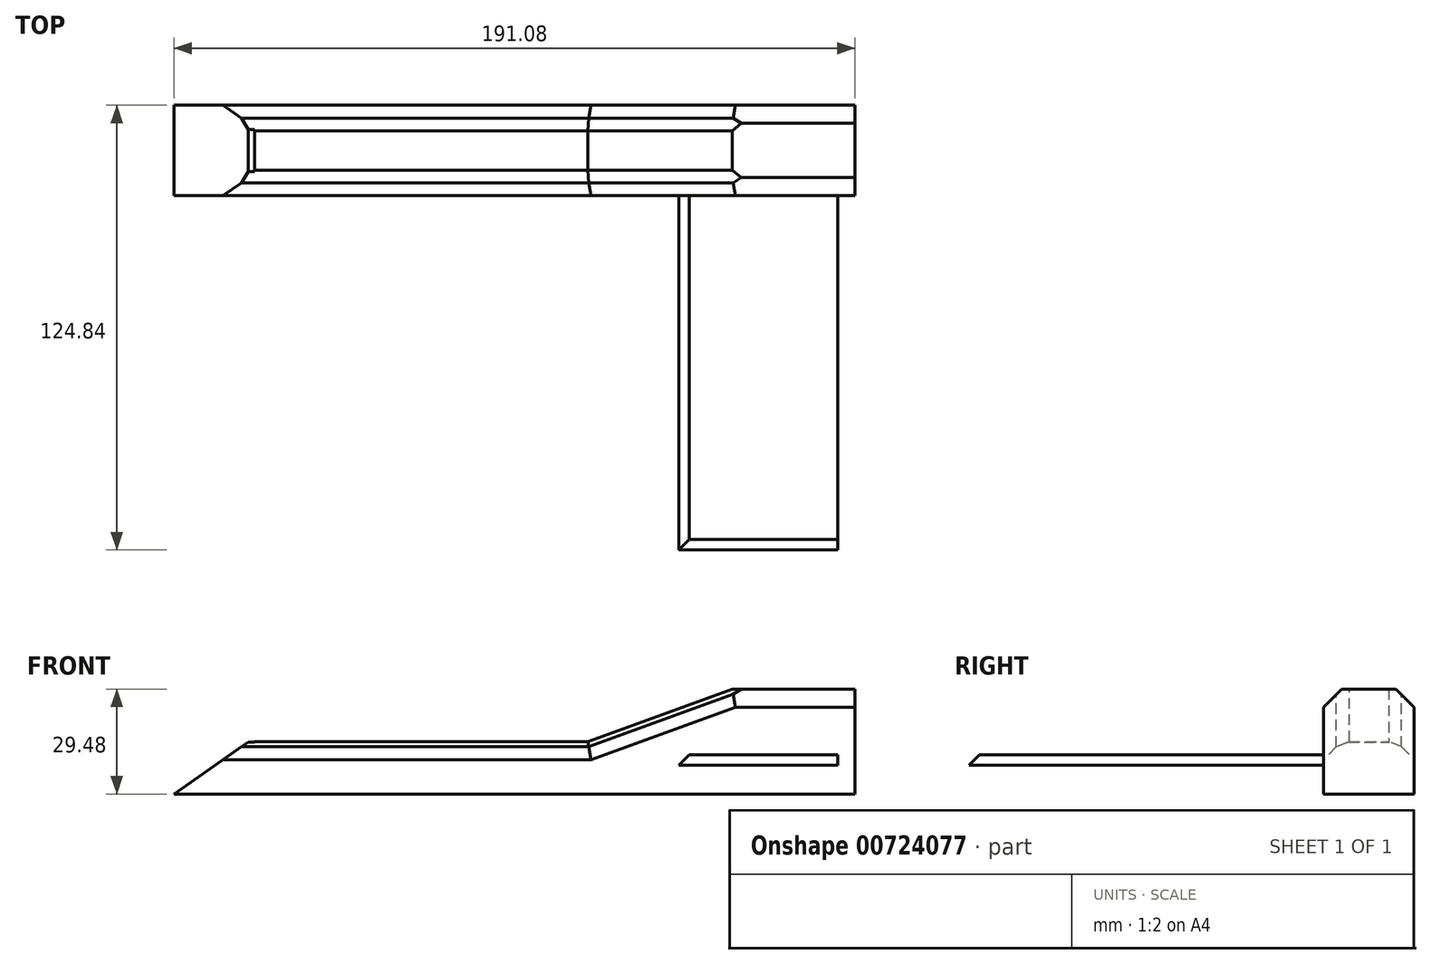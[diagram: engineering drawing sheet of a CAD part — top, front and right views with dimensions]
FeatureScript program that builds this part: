
annotation { "Feature Type Name" : "Feature", "Feature Type Description" : "" }
export const myFeature = defineFeature(function(context is Context, id is Id, definition is map)
    precondition{}
    {
        {
            var Q0;
            Q0=qCreatedBy(makeId("Front.planeOp"),FACE);
            var sketch = newSketch(context, id + "F0", { "sketchPlane" : qUnion([Q0])});
            skLineSegment(sketch, "E0.bottom", {"start": v(76.35, 0) * mm, "end": v(0, 0) * mm});
            skLineSegment(sketch, "E0.top", {"start": v(76.35, 29.48) * mm, "end": v(0, 29.48) * mm});
            skLineSegment(sketch, "E0.left", {"start": v(76.35, 0) * mm, "end": v(76.35, 29.48) * mm});
            skLineSegment(sketch, "E0.right", {"start": v(0, 0) * mm, "end": v(0, 29.48) * mm});
            skLineSegment(sketch, "E1.bottom", {"start": v(0, 14.74) * mm, "end": v(-92.14, 14.74) * mm});
            skLineSegment(sketch, "E1.top", {"start": v(0, 0) * mm, "end": v(-92.14, 0) * mm});
            skLineSegment(sketch, "E1.left", {"start": v(0, 14.74) * mm, "end": v(0, 0) * mm});
            skLineSegment(sketch, "E1.right", {"start": v(-92.14, 14.74) * mm, "end": v(-92.14, 0) * mm});
            skLineSegment(sketch, "E2.bottom", {"start": v(-92.14, 0) * mm, "end": v(-115.65, 0) * mm});
            skLineSegment(sketch, "E2.top", {"start": v(-92.14, 14.6) * mm, "end": v(-115.65, 14.6) * mm});
            skLineSegment(sketch, "E2.left", {"start": v(-92.14, 0) * mm, "end": v(-92.14, 14.6) * mm});
            skLineSegment(sketch, "E2.right", {"start": v(-115.65, 0) * mm, "end": v(-115.65, 14.6) * mm});
            skSolve(sketch);
        }
        {
            var Q0;
            Q0=makeQuery(id+"F0.imprint","IMPRINT",FACE,{"disambiguationData":[TD([[makeQuery(id+"F0.imprint","IMPRINT",EDGE,{"derivedFrom":sQuery(id+"F0.wireOp",EDGE,"E2.bottom")}),-1.0]])]});
            var Q1;
            Q1=makeQuery(id+"F0.imprint","IMPRINT",FACE,{"disambiguationData":[TD([[makeQuery(id+"F0.imprint","IMPRINT",EDGE,{"derivedFrom":sQuery(id+"F0.wireOp",EDGE,"E1.bottom")}),1.0]])]});
            var Q2;
            Q2=makeQuery(id+"F0.imprint","IMPRINT",FACE,{"disambiguationData":[TD([[makeQuery(id+"F0.imprint","IMPRINT",EDGE,{"derivedFrom":sQuery(id+"F0.wireOp",EDGE,"E0.bottom")}),-1.0]])]});
            extrude(context, id + "F1", {"entities" : qUnion([Q0, Q1, Q2]), "depth" : 25.4 * mm, "offsetDistance" : 25.4 * mm});
        }
        {
            var Q0;
            Q0=makeQuery(id+"F1.opExtrude","SWEPT_EDGE",EDGE,{"disambiguationData":[OSD([sQuery(id+"F0.wireOp",EDGE,"E0.top"),sQuery(id+"F0.wireOp",EDGE,"E0.right")])]});
            chamfer(context, id + "F2", {"entities" : qUnion([Q0]), "chamferType" : ChamferType.OFFSET_ANGLE, "width" : 15.24 * mm, "oppositeDirection" : false, "angle" : 70 * degree, "tangentPropagation" : true});
        }
        {
            var Q0;
            Q0=makeQuery(id+"F1.opExtrude","CAP_EDGE",EDGE,{"disambiguationData":[OSD([sQuery(id+"F0.wireOp",EDGE,"E1.bottom")])],"isStart":false});
            var Q1;
            Q1=makeQuery(id+"F1.opExtrude","CAP_EDGE",EDGE,{"disambiguationData":[OSD([sQuery(id+"F0.wireOp",EDGE,"E1.bottom")])],"isStart":true});
            var Q2;
            Q2=makeQuery(id+"F1.opExtrude","CAP_EDGE",EDGE,{"disambiguationData":[OSD([sQuery(id+"F0.wireOp",EDGE,"E0.top")])],"isStart":false});
            var Q3;
            {var subQ0=sQuery(id+"F0.wireOp",EDGE,"E0.right");var subQ1=sQuery(id+"F0.wireOp",EDGE,"E0.top");Q3=makeQuery(id+"F2.opChamfer","BLEND_EDGE",EDGE,{"blendedFrom":[makeQuery(id+"F1.opExtrude","SWEPT_EDGE",EDGE,{"disambiguationData":[OSD([subQ1,subQ0])]}),makeQuery(id+"F1.opExtrude","CAP_FACE",FACE,{"disambiguationData":[OSD([sQuery(id+"F0.wireOp",EDGE,"E0.bottom"),subQ1,sQuery(id+"F0.wireOp",EDGE,"E0.left"),subQ0,sQuery(id+"F0.wireOp",EDGE,"E1.bottom"),sQuery(id+"F0.wireOp",EDGE,"E1.top"),sQuery(id+"F0.wireOp",EDGE,"E1.right"),sQuery(id+"F0.wireOp",EDGE,"E2.bottom"),sQuery(id+"F0.wireOp",EDGE,"E2.top"),sQuery(id+"F0.wireOp",EDGE,"E2.right")])],"isStart":false})],"blendedInto":[makeQuery(id+"F1.opExtrude","CAP_FACE",FACE,{"disambiguationData":[OSD([sQuery(id+"F0.wireOp",EDGE,"E0.bottom"),subQ1,sQuery(id+"F0.wireOp",EDGE,"E0.left"),subQ0,sQuery(id+"F0.wireOp",EDGE,"E1.bottom"),sQuery(id+"F0.wireOp",EDGE,"E1.top"),sQuery(id+"F0.wireOp",EDGE,"E1.right"),sQuery(id+"F0.wireOp",EDGE,"E2.bottom"),sQuery(id+"F0.wireOp",EDGE,"E2.top"),sQuery(id+"F0.wireOp",EDGE,"E2.right")])],"isStart":false})]});}
            var Q4;
            {var subQ0=sQuery(id+"F0.wireOp",EDGE,"E0.right");var subQ1=sQuery(id+"F0.wireOp",EDGE,"E0.top");Q4=makeQuery(id+"F2.opChamfer","BLEND_EDGE",EDGE,{"blendedFrom":[makeQuery(id+"F1.opExtrude","SWEPT_EDGE",EDGE,{"disambiguationData":[OSD([subQ1,subQ0])]}),makeQuery(id+"F1.opExtrude","CAP_FACE",FACE,{"disambiguationData":[OSD([sQuery(id+"F0.wireOp",EDGE,"E0.bottom"),subQ1,sQuery(id+"F0.wireOp",EDGE,"E0.left"),subQ0,sQuery(id+"F0.wireOp",EDGE,"E1.bottom"),sQuery(id+"F0.wireOp",EDGE,"E1.top"),sQuery(id+"F0.wireOp",EDGE,"E1.right"),sQuery(id+"F0.wireOp",EDGE,"E2.bottom"),sQuery(id+"F0.wireOp",EDGE,"E2.top"),sQuery(id+"F0.wireOp",EDGE,"E2.right")])],"isStart":true})],"blendedInto":[makeQuery(id+"F1.opExtrude","CAP_FACE",FACE,{"disambiguationData":[OSD([sQuery(id+"F0.wireOp",EDGE,"E0.bottom"),subQ1,sQuery(id+"F0.wireOp",EDGE,"E0.left"),subQ0,sQuery(id+"F0.wireOp",EDGE,"E1.bottom"),sQuery(id+"F0.wireOp",EDGE,"E1.top"),sQuery(id+"F0.wireOp",EDGE,"E1.right"),sQuery(id+"F0.wireOp",EDGE,"E2.bottom"),sQuery(id+"F0.wireOp",EDGE,"E2.top"),sQuery(id+"F0.wireOp",EDGE,"E2.right")])],"isStart":true})]});}
            var Q5;
            Q5=makeQuery(id+"F1.opExtrude","CAP_EDGE",EDGE,{"disambiguationData":[OSD([sQuery(id+"F0.wireOp",EDGE,"E0.top")])],"isStart":true});
            chamfer(context, id + "F3", {"entities" : qUnion([Q0, Q1, Q2, Q3, Q4, Q5]), "width" : 5.08 * mm, "tangentPropagation" : true});
        }
        {
            var Q0;
            Q0=makeQuery(id+"F1.opExtrude","SWEPT_EDGE",EDGE,{"disambiguationData":[OSD([sQuery(id+"F0.wireOp",EDGE,"E2.top"),sQuery(id+"F0.wireOp",EDGE,"E2.right")])]});
            chamfer(context, id + "F4", {"entities" : qUnion([Q0]), "chamferType" : ChamferType.OFFSET_ANGLE, "width" : 15.24 * mm, "oppositeDirection" : false, "angle" : 55 * degree, "tangentPropagation" : true});
        }
        {
            var Q0;
            Q0=makeQuery(id+"F1.opExtrude","CAP_FACE",FACE,{"disambiguationData":[OSD([sQuery(id+"F0.wireOp",EDGE,"E0.bottom"),sQuery(id+"F0.wireOp",EDGE,"E0.top"),sQuery(id+"F0.wireOp",EDGE,"E0.left"),sQuery(id+"F0.wireOp",EDGE,"E0.right"),sQuery(id+"F0.wireOp",EDGE,"E1.bottom"),sQuery(id+"F0.wireOp",EDGE,"E1.top"),sQuery(id+"F0.wireOp",EDGE,"E1.right"),sQuery(id+"F0.wireOp",EDGE,"E2.bottom"),sQuery(id+"F0.wireOp",EDGE,"E2.top"),sQuery(id+"F0.wireOp",EDGE,"E2.right")])],"isStart":true});
            var sketch = newSketch(context, id + "F5", { "sketchPlane" : qUnion([Q0])});
            skLineSegment(sketch, "E3.bottom", {"start": v(-71.48, 10.95) * mm, "end": v(-24.76, 10.95) * mm});
            skLineSegment(sketch, "E3.top", {"start": v(-71.48, 8.03) * mm, "end": v(-24.76, 8.03) * mm});
            skLineSegment(sketch, "E3.left", {"start": v(-71.48, 10.95) * mm, "end": v(-71.48, 8.03) * mm});
            skLineSegment(sketch, "E3.right", {"start": v(-24.76, 10.95) * mm, "end": v(-24.76, 8.03) * mm});
            skSolve(sketch);
        }
        {
            var Q0;
            Q0=makeQuery(id+"F5.imprint","IMPRINT",FACE,{"disambiguationData":[TD([[makeQuery(id+"F5.imprint","IMPRINT",EDGE,{"derivedFrom":sQuery(id+"F5.wireOp",EDGE,"E3.bottom")}),-1.0]])]});
            extrude(context, id + "F6", {"entities" : qUnion([Q0]), "operationType" : NewBodyOperationType.ADD, "oppositeDirection" : true, "depth" : 127 * mm, "offsetDistance" : 25.4 * mm});
        }
        {
            var Q0;
            Q0=makeQuery(id+"F6.opExtrude","SWEPT_EDGE",EDGE,{"disambiguationData":[OSD([sQuery(id+"F5.wireOp",EDGE,"E3.bottom"),sQuery(id+"F5.wireOp",EDGE,"E3.right")])]});
            var Q1;
            Q1=makeQuery(id+"F6.opExtrude","CAP_EDGE",EDGE,{"disambiguationData":[OSD([sQuery(id+"F5.wireOp",EDGE,"E3.bottom")])],"isStart":false});
            var Q2;
            {var subQ0=sQuery(id+"F0.wireOp",EDGE,"E0.right");var subQ1=sQuery(id+"F0.wireOp",EDGE,"E0.top");Q2=makeQuery(id+"F3.opChamfer","BLEND_EDGE",EDGE,{"blendedFrom":[makeQuery(id+"F2.opChamfer","BLEND_EDGE",EDGE,{"blendedFrom":[makeQuery(id+"F1.opExtrude","SWEPT_EDGE",EDGE,{"disambiguationData":[OSD([subQ1,subQ0])]}),makeQuery(id+"F1.opExtrude","CAP_FACE",FACE,{"disambiguationData":[OSD([sQuery(id+"F0.wireOp",EDGE,"E0.bottom"),subQ1,sQuery(id+"F0.wireOp",EDGE,"E0.left"),subQ0,sQuery(id+"F0.wireOp",EDGE,"E1.bottom"),sQuery(id+"F0.wireOp",EDGE,"E1.top"),sQuery(id+"F0.wireOp",EDGE,"E1.right"),sQuery(id+"F0.wireOp",EDGE,"E2.bottom"),sQuery(id+"F0.wireOp",EDGE,"E2.top"),sQuery(id+"F0.wireOp",EDGE,"E2.right")])],"isStart":true})],"blendedInto":[makeQuery(id+"F1.opExtrude","CAP_FACE",FACE,{"disambiguationData":[OSD([sQuery(id+"F0.wireOp",EDGE,"E0.bottom"),subQ1,sQuery(id+"F0.wireOp",EDGE,"E0.left"),subQ0,sQuery(id+"F0.wireOp",EDGE,"E1.bottom"),sQuery(id+"F0.wireOp",EDGE,"E1.top"),sQuery(id+"F0.wireOp",EDGE,"E1.right"),sQuery(id+"F0.wireOp",EDGE,"E2.bottom"),sQuery(id+"F0.wireOp",EDGE,"E2.top"),sQuery(id+"F0.wireOp",EDGE,"E2.right")])],"isStart":true})]}),makeQuery(id+"F2.opChamfer","BLEND_FACE",FACE,{"disambiguationData":[OSD([subQ1,subQ0])]})],"blendedInto":[makeQuery(id+"F2.opChamfer","BLEND_FACE",FACE,{"disambiguationData":[OSD([subQ1,subQ0])]})]});}
            var Q3;
            {var subQ0=sQuery(id+"F0.wireOp",EDGE,"E1.bottom");Q3=makeQuery(id+"F3.opChamfer","BLEND_EDGE",EDGE,{"blendedFrom":[makeQuery(id+"F1.opExtrude","CAP_EDGE",EDGE,{"disambiguationData":[OSD([subQ0])],"isStart":true}),makeQuery(id+"F1.opExtrude","SWEPT_FACE",FACE,{"disambiguationData":[OSD([subQ0])]})],"blendedInto":[makeQuery(id+"F1.opExtrude","SWEPT_FACE",FACE,{"disambiguationData":[OSD([subQ0])]})]});}
            var Q4;
            {var subQ0=sQuery(id+"F0.wireOp",EDGE,"E1.bottom");Q4=makeQuery(id+"F3.opChamfer","BLEND_EDGE",EDGE,{"blendedFrom":[makeQuery(id+"F1.opExtrude","CAP_EDGE",EDGE,{"disambiguationData":[OSD([subQ0])],"isStart":false}),makeQuery(id+"F1.opExtrude","SWEPT_FACE",FACE,{"disambiguationData":[OSD([subQ0])]})],"blendedInto":[makeQuery(id+"F1.opExtrude","SWEPT_FACE",FACE,{"disambiguationData":[OSD([subQ0])]})]});}
            var Q5;
            {var subQ0=sQuery(id+"F0.wireOp",EDGE,"E0.right");var subQ1=sQuery(id+"F0.wireOp",EDGE,"E0.top");Q5=makeQuery(id+"F3.opChamfer","BLEND_EDGE",EDGE,{"blendedFrom":[makeQuery(id+"F2.opChamfer","BLEND_EDGE",EDGE,{"blendedFrom":[makeQuery(id+"F1.opExtrude","SWEPT_EDGE",EDGE,{"disambiguationData":[OSD([subQ1,subQ0])]}),makeQuery(id+"F1.opExtrude","CAP_FACE",FACE,{"disambiguationData":[OSD([sQuery(id+"F0.wireOp",EDGE,"E0.bottom"),subQ1,sQuery(id+"F0.wireOp",EDGE,"E0.left"),subQ0,sQuery(id+"F0.wireOp",EDGE,"E1.bottom"),sQuery(id+"F0.wireOp",EDGE,"E1.top"),sQuery(id+"F0.wireOp",EDGE,"E1.right"),sQuery(id+"F0.wireOp",EDGE,"E2.bottom"),sQuery(id+"F0.wireOp",EDGE,"E2.top"),sQuery(id+"F0.wireOp",EDGE,"E2.right")])],"isStart":false})],"blendedInto":[makeQuery(id+"F1.opExtrude","CAP_FACE",FACE,{"disambiguationData":[OSD([sQuery(id+"F0.wireOp",EDGE,"E0.bottom"),subQ1,sQuery(id+"F0.wireOp",EDGE,"E0.left"),subQ0,sQuery(id+"F0.wireOp",EDGE,"E1.bottom"),sQuery(id+"F0.wireOp",EDGE,"E1.top"),sQuery(id+"F0.wireOp",EDGE,"E1.right"),sQuery(id+"F0.wireOp",EDGE,"E2.bottom"),sQuery(id+"F0.wireOp",EDGE,"E2.top"),sQuery(id+"F0.wireOp",EDGE,"E2.right")])],"isStart":false})]}),makeQuery(id+"F2.opChamfer","BLEND_FACE",FACE,{"disambiguationData":[OSD([subQ1,subQ0])]})],"blendedInto":[makeQuery(id+"F2.opChamfer","BLEND_FACE",FACE,{"disambiguationData":[OSD([subQ1,subQ0])]})]});}
            chamfer(context, id + "F7", {"entities" : qUnion([Q0, Q1, Q2, Q3, Q4, Q5]), "width" : 5.08 * mm, "tangentPropagation" : true});
        }
    });
